# Revit family: Door-Sentry-Gate_BetweenJambMount_CornellIron
name_source: partatom
category: Doors
revit_build: Autodesk Revit MEP 2013 (Build: 20130531_2115(x64)
units: mm (PartAtom-declared; Revit-internal decimal feet)

## types (6) — shared parameters
04 CSI = 08 33 00
95 CSI = 08330
Assembly Code = B2030410
Coil Dimension Note = 11” to 14” - Consult Cornell when dimensions are critical.
Cost Note = Based on size, materials selected. Consult Cornell.
Crank Height = 6' - 8"
Curtain - Rods 2" OC Standard = Injection molded components with continuous metal rods spaced every two inches.
Description = Grille product with unique, injection molded components and continuous metal rods.
Distributor Locator = http://www.cornelliron.com
Function = Interior
Height = 10' - 0"
Jamb Dimension Note = 5 1/2” to 6 1/2” wide. Consult Cornell when dimensions are critical.
LEED Information = http://www.cornelliron.com
Manufacturer = Cornell Iron Works
Model = ESG21
Mounting = Between Jambs
Operator Width = 10' - 3"
Optional aluminum, color anodized finish = No
Product Options = SG3 model ESG20, when countertop or compact components are desired. Black or white matte curtain components.
Representatives Disclaimer = Cornell products are sold and installed through a nationwide network of independent distributors.
Revit Object Download Link = http://cornellcookson.smartbim.com
Sizing Disclaimer = Openings up to 21’ wide x 10’ high standard construction. Smaller / countertop SentryGate 3 model also available.
Subcategory = Overhead Doors
URL = http://www.cornelliron.com
URL CAD = http://www.cornelliron.com
URL Photographs = http://www.cornelliron.com
URL Specifications = http://www.cornelliron.com
Wall Closure = By host
Wall Construction = Drywall, wood, masonry, steel
Width = 10' - 0"

## per-type parameters (varying)
| type | Bottom Bar | From Coil Side Operate on Left | From Coil Side Operate on Right | Guides | Hand Crank | Hood | Motor | Operator | Push Up |
| Motor Operated, Aluminium (Anodized Finish) | Aluminum, anodized finish (non-curtain components) | No | Yes | Aluminum, anodized finish (non-curtain components) | No | Aluminum, anodized finish (non-curtain components) | Yes | Operator : Motor Operated | No |
| Hand-Crank Operated, Aluminium (Anodized Finish) | Aluminum, anodized finish (non-curtain components) | No | Yes | Aluminum, anodized finish (non-curtain components) | Yes | Aluminum, anodized finish (non-curtain components) | No | Operator : Hand-Crank | No |
| Push-Up Operated, Aluminium (Anodized Finish) | Aluminum, anodized finish (non-curtain components) | No | Yes | Aluminum, anodized finish (non-curtain components) | No | Aluminum, anodized finish (non-curtain components) | No | Operator : Push-UP | Yes |
| Hand-Crank Operated, Aluminium (Mill Finish) | Aluminum, mill finish (non curtain components) | Yes | No | Aluminum, mill finish (non curtain components) | Yes | Aluminum, mill finish (non curtain components) | No | Operator : Hand-Crank | No |
| Motor Operated, Aluminium (Mill Finish) | Aluminum, mill finish (non curtain components) | No | Yes | Aluminum, mill finish (non curtain components) | No | Aluminum, mill finish (non curtain components) | Yes | Operator : Motor Operated | No |
| Push-Up Operated, Aluminium (Mill Finish) | Aluminum, mill finish (non curtain components) | No | Yes | Aluminum, mill finish (non curtain components) | No | Aluminum, mill finish (non curtain components) | No | Operator : Push-UP | Yes |

## geometry (parser evidence)
native form markers: Blend x16, Sweep x12
no freeform markers — native parametric forms only
